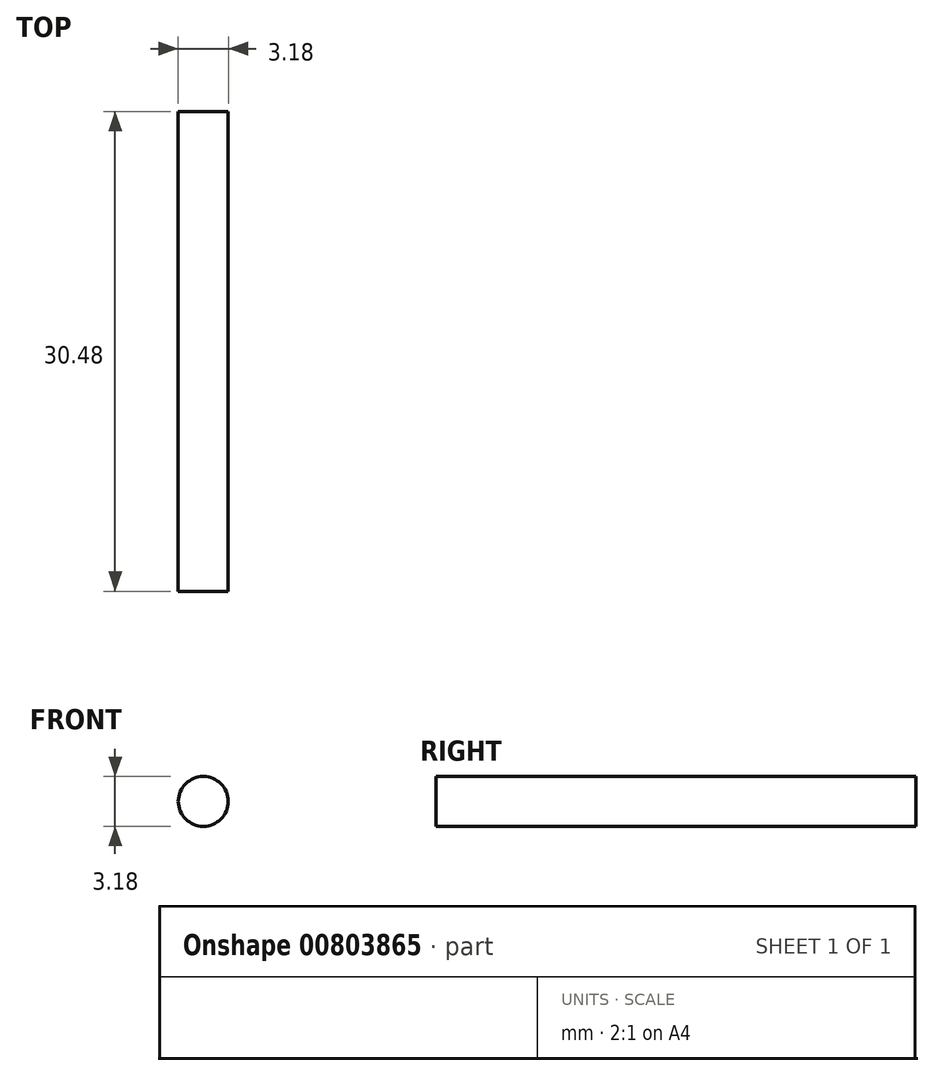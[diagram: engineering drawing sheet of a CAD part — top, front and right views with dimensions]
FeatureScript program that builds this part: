
annotation { "Feature Type Name" : "Feature", "Feature Type Description" : "" }
export const myFeature = defineFeature(function(context is Context, id is Id, definition is map)
    precondition{}
    {
        {
            var Q0;
            Q0=qCreatedBy(makeId("Front.planeOp"),FACE);
            var sketch = newSketch(context, id + "F0", { "sketchPlane" : qUnion([Q0])});
            skCircle(sketch, "E0", {"center": v(0, 0) * mm, "radius": 1.59 * mm});
            skSolve(sketch);
        }
        {
            var Q0;
            Q0=makeQuery(id+"F0.imprint","IMPRINT",FACE,{"disambiguationData":[TD([[makeQuery(id+"F0.imprint","IMPRINT",EDGE,{"derivedFrom":sQuery(id+"F0.wireOp",EDGE,"E0")}),1.0]])]});
            extrude(context, id + "F1", {"entities" : qUnion([Q0]), "depth" : 30.48 * mm, "offsetDistance" : 25.4 * mm});
        }
    });
